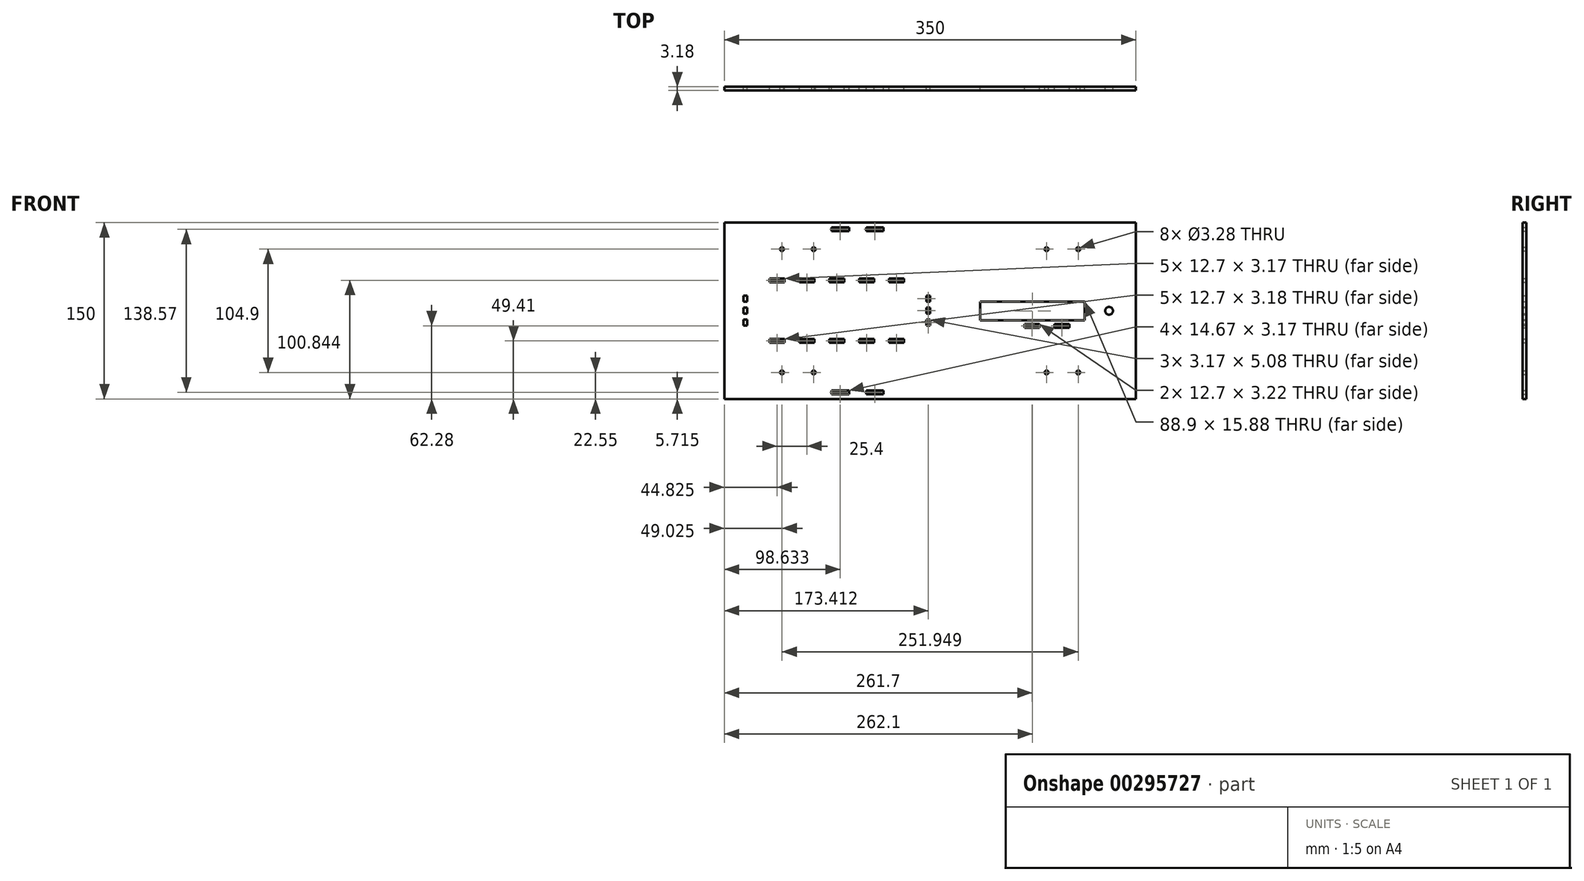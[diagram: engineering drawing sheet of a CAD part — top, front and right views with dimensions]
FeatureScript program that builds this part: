
annotation { "Feature Type Name" : "Feature", "Feature Type Description" : "" }
export const myFeature = defineFeature(function(context is Context, id is Id, definition is map)
    precondition{}
    {
        {
            var Q0;
            Q0=qCreatedBy(makeId("Front.planeOp"),FACE);
            var sketch = newSketch(context, id + "F0", { "sketchPlane" : qUnion([Q0])});
            skLineSegment(sketch, "E0.bottom", {"start": v(175, -75) * mm, "end": v(-175, -75) * mm});
            skLineSegment(sketch, "E0.top", {"start": v(175, 75) * mm, "end": v(-175, 75) * mm});
            skLineSegment(sketch, "E0.left", {"start": v(175, -75) * mm, "end": v(175, 75) * mm});
            skLineSegment(sketch, "E0.right", {"start": v(-175, -75) * mm, "end": v(-175, 75) * mm});
            skPoint(sketch, "E0.middle", {"position": v(0, 0) * mm});
            skCircle(sketch, "E1", {"center": v(-112.5, 52.45) * mm, "radius": 4 * mm, "construction": true});
            skLineSegment(sketch, "E2", {"start": v(-112.5, 52.45) * mm, "end": v(-108.5, 52.45) * mm, "construction": true});
            skLineSegment(sketch, "E3", {"start": v(-112.5, 52.45) * mm, "end": v(-112.5, 56.45) * mm, "construction": true});
            skCircle(sketch, "E4", {"center": v(-99.03, 52.45) * mm, "radius": 1.64 * mm});
            skCircle(sketch, "E5.MirrorC", {"center": v(-125.97, 52.45) * mm, "radius": 1.64 * mm});
            skCircle(sketch, "E6", {"center": v(-112.5, -52.45) * mm, "radius": 4 * mm, "construction": true});
            skLineSegment(sketch, "E7", {"start": v(-112.5, -52.45) * mm, "end": v(-108.5, -52.45) * mm, "construction": true});
            skLineSegment(sketch, "E8", {"start": v(-112.5, -52.45) * mm, "end": v(-112.5, -48.45) * mm, "construction": true});
            skCircle(sketch, "E9", {"center": v(-99.03, -52.45) * mm, "radius": 1.64 * mm});
            skCircle(sketch, "E10.MirrorC", {"center": v(-125.97, -52.45) * mm, "radius": 1.64 * mm});
            skCircle(sketch, "E11", {"center": v(112.5, -52.45) * mm, "radius": 4 * mm, "construction": true});
            skLineSegment(sketch, "E12", {"start": v(112.5, -52.45) * mm, "end": v(116.5, -52.45) * mm, "construction": true});
            skLineSegment(sketch, "E13", {"start": v(112.5, -52.45) * mm, "end": v(112.5, -48.45) * mm, "construction": true});
            skCircle(sketch, "E14", {"center": v(125.97, -52.45) * mm, "radius": 1.64 * mm});
            skCircle(sketch, "E15.MirrorC", {"center": v(99.03, -52.45) * mm, "radius": 1.64 * mm});
            skCircle(sketch, "E16", {"center": v(112.5, 52.45) * mm, "radius": 4 * mm, "construction": true});
            skLineSegment(sketch, "E17", {"start": v(112.5, 52.45) * mm, "end": v(116.5, 52.45) * mm, "construction": true});
            skLineSegment(sketch, "E18", {"start": v(112.5, 52.45) * mm, "end": v(112.5, 56.45) * mm, "construction": true});
            skCircle(sketch, "E19", {"center": v(125.97, 52.45) * mm, "radius": 1.64 * mm});
            skCircle(sketch, "E20.MirrorC", {"center": v(99.03, 52.45) * mm, "radius": 1.64 * mm});
            skLineSegment(sketch, "E21.bottom", {"start": v(-69.03, -70.87) * mm, "end": v(-83.7, -70.87) * mm});
            skLineSegment(sketch, "E21.top", {"start": v(-69.03, -67.7) * mm, "end": v(-83.7, -67.7) * mm});
            skLineSegment(sketch, "E21.left", {"start": v(-69.03, -70.87) * mm, "end": v(-69.03, -67.7) * mm});
            skLineSegment(sketch, "E21.right", {"start": v(-83.7, -70.87) * mm, "end": v(-83.7, -67.7) * mm});
            skPoint(sketch, "E21.middle", {"position": v(-76.37, -69.28) * mm});
            skLineSegment(sketch, "E22.bottom", {"start": v(-39.7, -70.87) * mm, "end": v(-54.37, -70.87) * mm});
            skLineSegment(sketch, "E22.top", {"start": v(-39.7, -67.7) * mm, "end": v(-54.37, -67.7) * mm});
            skLineSegment(sketch, "E22.left", {"start": v(-39.7, -70.87) * mm, "end": v(-39.7, -67.7) * mm});
            skLineSegment(sketch, "E22.right", {"start": v(-54.37, -70.87) * mm, "end": v(-54.37, -67.7) * mm});
            skPoint(sketch, "E22.middle", {"position": v(-47.03, -69.28) * mm});
            skLineSegment(sketch, "E23.bottom", {"start": v(-74.4, -81.35) * mm, "end": v(-150.6, -81.35) * mm, "construction": true});
            skLineSegment(sketch, "E23.top", {"start": v(-74.4, -75) * mm, "end": v(-150.6, -75) * mm, "construction": true});
            skLineSegment(sketch, "E23.left", {"start": v(-74.4, -81.35) * mm, "end": v(-74.4, -75) * mm, "construction": true});
            skLineSegment(sketch, "E23.right", {"start": v(-150.6, -81.35) * mm, "end": v(-150.6, -75) * mm, "construction": true});
            skPoint(sketch, "E23.middle", {"position": v(-112.5, -78.17) * mm});
            skPoint(sketch, "E23.middle.positionSnap0", {"position": v(-112.5, -50.45) * mm});
            skPoint(sketch, "E23.centerSnap0", {"position": v(-112.5, -50.45) * mm});
            skLineSegment(sketch, "E24.bottom", {"start": v(-74.4, -75) * mm, "end": v(-49, -75) * mm, "construction": true});
            skLineSegment(sketch, "E24.top", {"start": v(-74.4, -81.35) * mm, "end": v(-49, -81.35) * mm, "construction": true});
            skLineSegment(sketch, "E24.left", {"start": v(-74.4, -75) * mm, "end": v(-74.4, -81.35) * mm, "construction": true});
            skLineSegment(sketch, "E24.right", {"start": v(-49, -75) * mm, "end": v(-49, -81.35) * mm, "construction": true});
            skLineSegment(sketch, "E25", {"start": v(-69.03, -67.7) * mm, "end": v(-54.37, -70.87) * mm, "construction": true});
            skPoint(sketch, "E26", {"position": v(-61.7, -69.28) * mm});
            skPoint(sketch, "E27", {"position": v(-61.7, -75) * mm});
            skLineSegment(sketch, "E28", {"start": v(-61.7, -75) * mm, "end": v(-61.7, -81.35) * mm, "construction": true});
            skLineSegment(sketch, "E29.MirrorCS", {"start": v(-74.4, 75) * mm, "end": v(-150.6, 75) * mm, "construction": true});
            skLineSegment(sketch, "E30.MirrorCS", {"start": v(-74.4, 75) * mm, "end": v(-49, 75) * mm, "construction": true});
            skLineSegment(sketch, "E31.MirrorCS", {"start": v(-74.4, 81.35) * mm, "end": v(-150.6, 81.35) * mm, "construction": true});
            skLineSegment(sketch, "E32.MirrorCS", {"start": v(-150.6, 81.35) * mm, "end": v(-150.6, 75) * mm, "construction": true});
            skLineSegment(sketch, "E33.MirrorCS", {"start": v(-74.4, 81.35) * mm, "end": v(-49, 81.35) * mm, "construction": true});
            skLineSegment(sketch, "E34.MirrorCS", {"start": v(-74.4, 75) * mm, "end": v(-74.4, 81.35) * mm, "construction": true});
            skLineSegment(sketch, "E35.MirrorCS", {"start": v(-61.7, 75) * mm, "end": v(-61.7, 81.35) * mm, "construction": true});
            skLineSegment(sketch, "E36.MirrorCS", {"start": v(-49, 75) * mm, "end": v(-49, 81.35) * mm, "construction": true});
            skLineSegment(sketch, "E37.MirrorCS", {"start": v(-39.7, 70.87) * mm, "end": v(-54.37, 70.87) * mm});
            skLineSegment(sketch, "E38.MirrorCS", {"start": v(-54.37, 70.87) * mm, "end": v(-54.37, 67.7) * mm});
            skLineSegment(sketch, "E39.MirrorCS", {"start": v(-39.7, 67.7) * mm, "end": v(-54.37, 67.7) * mm});
            skLineSegment(sketch, "E40.MirrorCS", {"start": v(-39.7, 70.87) * mm, "end": v(-39.7, 67.7) * mm});
            skLineSegment(sketch, "E41.MirrorCS", {"start": v(-69.03, 70.87) * mm, "end": v(-69.03, 67.7) * mm});
            skLineSegment(sketch, "E42.MirrorCS", {"start": v(-69.03, 67.7) * mm, "end": v(-83.7, 67.7) * mm});
            skLineSegment(sketch, "E43.MirrorCS", {"start": v(-83.7, 70.87) * mm, "end": v(-83.7, 67.7) * mm});
            skLineSegment(sketch, "E44.MirrorCS", {"start": v(-69.03, 70.87) * mm, "end": v(-83.7, 70.87) * mm});
            skLineSegment(sketch, "E45.MirrorCS", {"start": v(-69.03, 67.7) * mm, "end": v(-54.37, 70.87) * mm, "construction": true});
            skPoint(sketch, "E46.middle", {"position": v(-79.38, 0.13) * mm});
            skLineSegment(sketch, "E47.top", {"start": v(-3.18, -12.57) * mm, "end": v(-3.18, -7.5) * mm});
            skLineSegment(sketch, "E47.left", {"start": v(0, -12.57) * mm, "end": v(-3.18, -12.57) * mm});
            skLineSegment(sketch, "E47.right", {"start": v(0, -7.5) * mm, "end": v(-3.18, -7.5) * mm});
            skLineSegment(sketch, "E48.left", {"start": v(-3.18, -7.5) * mm, "end": v(0, -7.5) * mm});
            skLineSegment(sketch, "E48.right", {"start": v(-3.18, -2.41) * mm, "end": v(0, -2.41) * mm});
            skLineSegment(sketch, "E49.top", {"start": v(-3.18, -2.41) * mm, "end": v(-3.18, 2.67) * mm});
            skLineSegment(sketch, "E49.left", {"start": v(0, -2.41) * mm, "end": v(-3.18, -2.41) * mm});
            skLineSegment(sketch, "E49.right", {"start": v(0, 2.67) * mm, "end": v(-3.18, 2.67) * mm});
            skLineSegment(sketch, "E50.left", {"start": v(-3.18, 2.67) * mm, "end": v(0, 2.67) * mm});
            skLineSegment(sketch, "E50.right", {"start": v(-3.18, 7.75) * mm, "end": v(0, 7.75) * mm});
            skLineSegment(sketch, "E51.top", {"start": v(-3.18, 12.83) * mm, "end": v(-3.18, 7.75) * mm});
            skLineSegment(sketch, "E51.left", {"start": v(0, 12.83) * mm, "end": v(-3.18, 12.83) * mm});
            skLineSegment(sketch, "E51.right", {"start": v(0, 7.75) * mm, "end": v(-3.18, 7.75) * mm});
            skLineSegment(sketch, "E52.MirrorCS", {"start": v(-158.75, -12.57) * mm, "end": v(-155.58, -12.57) * mm});
            skLineSegment(sketch, "E53.MirrorCS", {"start": v(-155.58, -12.57) * mm, "end": v(-155.58, -7.5) * mm});
            skLineSegment(sketch, "E54.MirrorCS", {"start": v(-158.75, -7.5) * mm, "end": v(-155.58, -7.5) * mm});
            skLineSegment(sketch, "E55.MirrorCS", {"start": v(-155.58, -2.41) * mm, "end": v(-158.75, -2.41) * mm});
            skLineSegment(sketch, "E56.MirrorCS", {"start": v(-155.58, -2.41) * mm, "end": v(-155.58, 2.67) * mm});
            skLineSegment(sketch, "E57.MirrorCS", {"start": v(-158.75, 2.67) * mm, "end": v(-155.58, 2.67) * mm});
            skLineSegment(sketch, "E58.MirrorCS", {"start": v(-155.58, 7.75) * mm, "end": v(-158.75, 7.75) * mm});
            skLineSegment(sketch, "E59.MirrorCS", {"start": v(-155.58, 12.83) * mm, "end": v(-155.58, 7.75) * mm});
            skLineSegment(sketch, "E60.MirrorCS", {"start": v(-158.75, 12.83) * mm, "end": v(-155.58, 12.83) * mm});
            skLineSegment(sketch, "E61.bottom", {"start": v(-73.03, 24.26) * mm, "end": v(-73.03, 27.43) * mm});
            skLineSegment(sketch, "E61.top", {"start": v(-85.73, 24.26) * mm, "end": v(-85.73, 27.43) * mm});
            skLineSegment(sketch, "E61.left", {"start": v(-73.03, 24.26) * mm, "end": v(-85.73, 24.26) * mm});
            skLineSegment(sketch, "E62.bottom", {"start": v(-85.73, 27.43) * mm, "end": v(-85.73, 24.26) * mm});
            skLineSegment(sketch, "E62.top", {"start": v(-98.43, 27.43) * mm, "end": v(-98.43, 24.26) * mm});
            skLineSegment(sketch, "E63.bottom", {"start": v(-98.43, 24.26) * mm, "end": v(-98.43, 27.43) * mm});
            skLineSegment(sketch, "E63.top", {"start": v(-111.13, 24.26) * mm, "end": v(-111.13, 27.43) * mm});
            skLineSegment(sketch, "E63.left", {"start": v(-98.43, 24.26) * mm, "end": v(-111.13, 24.26) * mm});
            skLineSegment(sketch, "E64.bottom", {"start": v(-111.13, 27.43) * mm, "end": v(-111.13, 24.26) * mm});
            skLineSegment(sketch, "E64.top", {"start": v(-123.83, 27.43) * mm, "end": v(-123.83, 24.26) * mm});
            skLineSegment(sketch, "E65.bottom", {"start": v(-123.83, 24.26) * mm, "end": v(-123.83, 27.43) * mm});
            skLineSegment(sketch, "E65.top", {"start": v(-136.53, 24.26) * mm, "end": v(-136.53, 27.43) * mm});
            skLineSegment(sketch, "E65.left", {"start": v(-123.83, 24.26) * mm, "end": v(-136.53, 24.26) * mm});
            skLineSegment(sketch, "E66.MirrorCS", {"start": v(-60.33, 27.43) * mm, "end": v(-60.33, 24.26) * mm});
            skLineSegment(sketch, "E67.MirrorCS", {"start": v(-34.93, 24.26) * mm, "end": v(-34.93, 27.43) * mm});
            skLineSegment(sketch, "E68.MirrorCS", {"start": v(-47.63, 27.43) * mm, "end": v(-47.63, 24.26) * mm});
            skLineSegment(sketch, "E69.MirrorCS", {"start": v(-34.93, 27.43) * mm, "end": v(-34.93, 24.26) * mm});
            skLineSegment(sketch, "E70.MirrorCS", {"start": v(-47.63, 24.26) * mm, "end": v(-47.63, 27.43) * mm});
            skLineSegment(sketch, "E71.MirrorCS", {"start": v(-60.33, 24.26) * mm, "end": v(-60.33, 27.43) * mm});
            skLineSegment(sketch, "E72.MirrorCS", {"start": v(-22.22, 24.26) * mm, "end": v(-22.22, 27.43) * mm});
            skLineSegment(sketch, "E73.MirrorCS", {"start": v(-34.93, 24.26) * mm, "end": v(-22.22, 24.26) * mm});
            skLineSegment(sketch, "E74.MirrorCS", {"start": v(-60.33, 24.26) * mm, "end": v(-47.63, 24.26) * mm});
            skLineSegment(sketch, "E75.MirrorCS", {"start": v(-98.43, -27.18) * mm, "end": v(-98.43, -24) * mm});
            skLineSegment(sketch, "E76.MirrorCS", {"start": v(-60.33, -24) * mm, "end": v(-60.33, -27.18) * mm});
            skLineSegment(sketch, "E77.MirrorCS", {"start": v(-47.63, -27.18) * mm, "end": v(-47.63, -24) * mm});
            skLineSegment(sketch, "E78.MirrorCS", {"start": v(-85.73, -24) * mm, "end": v(-85.73, -27.18) * mm});
            skLineSegment(sketch, "E79.MirrorCS", {"start": v(-123.83, -27.18) * mm, "end": v(-123.83, -24) * mm});
            skLineSegment(sketch, "E80.MirrorCS", {"start": v(-111.13, -24) * mm, "end": v(-111.13, -27.18) * mm});
            skLineSegment(sketch, "E81.MirrorCS", {"start": v(-34.93, -27.18) * mm, "end": v(-34.93, -24) * mm});
            skLineSegment(sketch, "E82.MirrorCS", {"start": v(-123.83, -24) * mm, "end": v(-123.83, -27.18) * mm});
            skLineSegment(sketch, "E83.MirrorCS", {"start": v(-85.73, -27.18) * mm, "end": v(-85.73, -24) * mm});
            skLineSegment(sketch, "E84.MirrorCS", {"start": v(-34.93, -24) * mm, "end": v(-34.93, -27.18) * mm});
            skLineSegment(sketch, "E85.MirrorCS", {"start": v(-111.13, -27.18) * mm, "end": v(-111.13, -24) * mm});
            skLineSegment(sketch, "E86.MirrorCS", {"start": v(-47.63, -24) * mm, "end": v(-47.63, -27.18) * mm});
            skLineSegment(sketch, "E87.MirrorCS", {"start": v(-60.33, -27.18) * mm, "end": v(-60.33, -24) * mm});
            skLineSegment(sketch, "E88.MirrorCS", {"start": v(-98.43, -24) * mm, "end": v(-98.43, -27.18) * mm});
            skLineSegment(sketch, "E89.MirrorCS", {"start": v(-73.03, -24) * mm, "end": v(-73.03, -27.18) * mm});
            skLineSegment(sketch, "E90.MirrorCS", {"start": v(-136.53, -24) * mm, "end": v(-136.53, -27.18) * mm});
            skLineSegment(sketch, "E91.MirrorCS", {"start": v(-22.22, -24) * mm, "end": v(-22.22, -27.18) * mm});
            skLineSegment(sketch, "E92.MirrorCS", {"start": v(-73.03, -24) * mm, "end": v(-85.73, -24) * mm});
            skLineSegment(sketch, "E93.MirrorCS", {"start": v(-123.83, -24) * mm, "end": v(-136.53, -24) * mm});
            skLineSegment(sketch, "E94.MirrorCS", {"start": v(-60.33, -24) * mm, "end": v(-47.63, -24) * mm});
            skLineSegment(sketch, "E95.MirrorCS", {"start": v(-98.43, -24) * mm, "end": v(-111.13, -24) * mm});
            skLineSegment(sketch, "E96.MirrorCS", {"start": v(-34.93, -24) * mm, "end": v(-22.22, -24) * mm});
            skLineSegment(sketch, "E97", {"start": v(-158.75, 12.83) * mm, "end": v(-158.75, 7.75) * mm});
            skLineSegment(sketch, "E98", {"start": v(-158.75, 2.67) * mm, "end": v(-158.75, -2.41) * mm});
            skLineSegment(sketch, "E99", {"start": v(-158.75, -7.5) * mm, "end": v(-158.75, -12.57) * mm});
            skLineSegment(sketch, "E100", {"start": v(-136.53, 27.43) * mm, "end": v(-123.83, 27.43) * mm});
            skLineSegment(sketch, "E101", {"start": v(-111.13, 27.43) * mm, "end": v(-98.43, 27.43) * mm});
            skLineSegment(sketch, "E102", {"start": v(-85.73, 27.43) * mm, "end": v(-73.03, 27.43) * mm});
            skLineSegment(sketch, "E103", {"start": v(-60.33, 27.43) * mm, "end": v(-47.63, 27.43) * mm});
            skLineSegment(sketch, "E104", {"start": v(-34.93, 27.43) * mm, "end": v(-22.22, 27.43) * mm});
            skLineSegment(sketch, "E105", {"start": v(0, 12.83) * mm, "end": v(0, 7.75) * mm});
            skLineSegment(sketch, "E106", {"start": v(0, 2.67) * mm, "end": v(0, -2.41) * mm});
            skLineSegment(sketch, "E107", {"start": v(0, -7.5) * mm, "end": v(0, -12.57) * mm});
            skLineSegment(sketch, "E108", {"start": v(-22.22, -27.18) * mm, "end": v(-34.93, -27.18) * mm});
            skLineSegment(sketch, "E109", {"start": v(-47.63, -27.18) * mm, "end": v(-60.33, -27.18) * mm});
            skLineSegment(sketch, "E110", {"start": v(-73.03, -27.18) * mm, "end": v(-85.73, -27.18) * mm});
            skLineSegment(sketch, "E111", {"start": v(-98.43, -27.18) * mm, "end": v(-111.13, -27.18) * mm});
            skLineSegment(sketch, "E112", {"start": v(-123.83, -27.18) * mm, "end": v(-136.53, -27.18) * mm});
            skLineSegment(sketch, "E113", {"start": v(112.5, 52.45) * mm, "end": v(112.5, -52.45) * mm, "construction": true});
            skLineSegment(sketch, "E114", {"start": v(112.5, 0) * mm, "end": v(51.32, 0) * mm, "construction": true});
            skPoint(sketch, "E114.endSnap0", {"position": v(112.5, 0) * mm});
            skLineSegment(sketch, "E115.bottom", {"start": v(131.55, -7.94) * mm, "end": v(93.45, -7.94) * mm});
            skLineSegment(sketch, "E115.top", {"start": v(131.55, 7.94) * mm, "end": v(93.45, 7.94) * mm});
            skLineSegment(sketch, "E115.left", {"start": v(131.55, -7.94) * mm, "end": v(131.55, 7.94) * mm});
            skLineSegment(sketch, "E115.right", {"start": v(93.45, -7.94) * mm, "end": v(93.45, 7.94) * mm});
            skLineSegment(sketch, "E116", {"start": v(112.5, 0) * mm, "end": v(175, 0) * mm, "construction": true});
            skLineSegment(sketch, "E117.MirrorCS", {"start": v(55.35, -7.94) * mm, "end": v(93.45, -7.94) * mm});
            skLineSegment(sketch, "E118.MirrorCS", {"start": v(55.35, 7.94) * mm, "end": v(93.45, 7.94) * mm});
            skLineSegment(sketch, "E119.MirrorCS", {"start": v(55.35, -7.94) * mm, "end": v(55.35, 7.94) * mm});
            skLineSegment(sketch, "E120.MirrorCS", {"start": v(93.05, -11.11) * mm, "end": v(93.05, -14.33) * mm});
            skLineSegment(sketch, "E121.MirrorCS", {"start": v(105.75, -11.11) * mm, "end": v(105.75, -14.33) * mm});
            skLineSegment(sketch, "E122.MirrorCS", {"start": v(80.35, -11.11) * mm, "end": v(80.35, -14.33) * mm});
            skLineSegment(sketch, "E123.MirrorCS", {"start": v(93.05, -14.33) * mm, "end": v(80.35, -14.33) * mm});
            skLineSegment(sketch, "E124.MirrorCS", {"start": v(118.45, -14.33) * mm, "end": v(105.75, -14.33) * mm});
            skLineSegment(sketch, "E125.MirrorCS", {"start": v(93.05, -11.11) * mm, "end": v(80.35, -11.11) * mm});
            skLineSegment(sketch, "E126.MirrorCS", {"start": v(93.05, -14.33) * mm, "end": v(93.05, -11.11) * mm});
            skLineSegment(sketch, "E127.MirrorCS", {"start": v(118.45, -11.11) * mm, "end": v(105.75, -11.11) * mm});
            skLineSegment(sketch, "E128.MirrorCS", {"start": v(105.75, -14.33) * mm, "end": v(105.75, -11.11) * mm});
            skLineSegment(sketch, "E129.MirrorCS", {"start": v(118.45, -11.11) * mm, "end": v(118.45, -14.33) * mm});
            skLineSegment(sketch, "E130", {"start": v(42.65, 7.94) * mm, "end": v(42.65, -7.94) * mm});
            skLineSegment(sketch, "E131", {"start": v(42.65, 7.94) * mm, "end": v(55.35, 7.94) * mm});
            skLineSegment(sketch, "E132", {"start": v(42.65, -7.94) * mm, "end": v(55.35, -7.94) * mm});
            skCircle(sketch, "E133", {"center": v(152.14, 0) * mm, "radius": 3.3 * mm});
            skSolve(sketch);
        }
        {
            var Q0;
            Q0=qSketchRegion(id+"F0",true);
            extrude(context, id + "F1", {"entities" : qUnion([Q0]), "depth" : 3.17 * mm});
        }
    });
